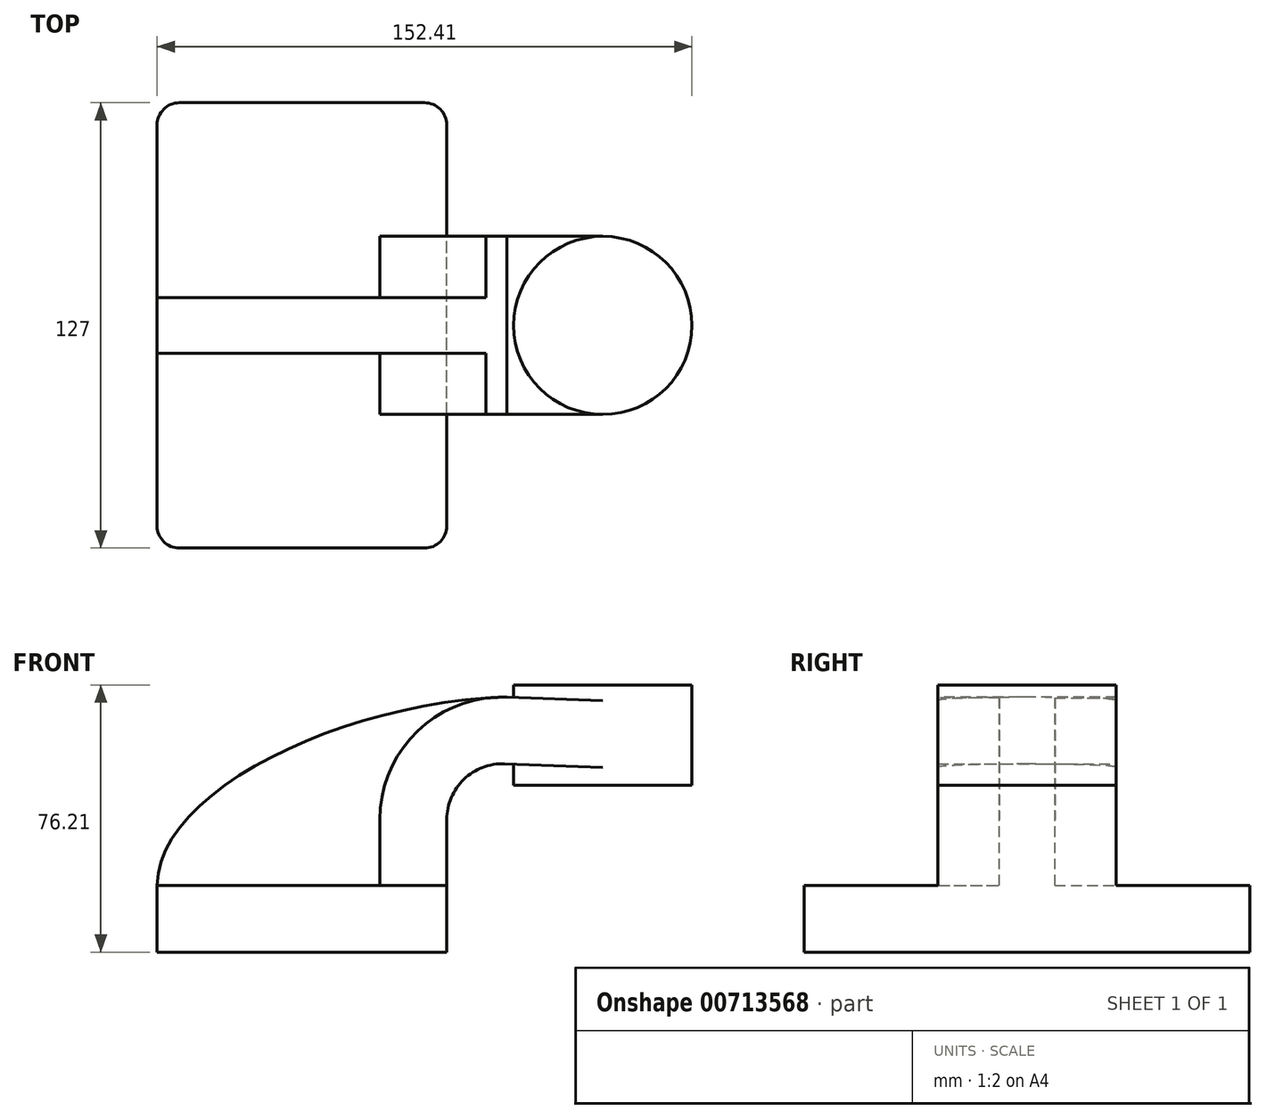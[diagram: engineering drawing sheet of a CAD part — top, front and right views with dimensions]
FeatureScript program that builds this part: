
annotation { "Feature Type Name" : "Feature", "Feature Type Description" : "" }
export const myFeature = defineFeature(function(context is Context, id is Id, definition is map)
    precondition{}
    {
        {
            var Q0;
            Q0=qCreatedBy(makeId("Front.planeOp"),FACE);
            var sketch = newSketch(context, id + "F0", { "sketchPlane" : qUnion([Q0])});
            skLineSegment(sketch, "E0.bottom", {"start": v(-41.28, -9.53) * mm, "end": v(41.28, -9.53) * mm});
            skLineSegment(sketch, "E0.top", {"start": v(-41.28, 9.53) * mm, "end": v(41.28, 9.53) * mm});
            skLineSegment(sketch, "E0.left", {"start": v(-41.28, -9.53) * mm, "end": v(-41.28, 9.53) * mm});
            skLineSegment(sketch, "E0.right", {"start": v(41.28, -9.53) * mm, "end": v(41.28, 9.53) * mm});
            skPoint(sketch, "E0.middle", {"position": v(0, 0) * mm});
            skLineSegment(sketch, "E1.bottom", {"start": v(60.33, 38.1) * mm, "end": v(111.13, 38.1) * mm});
            skLineSegment(sketch, "E1.top", {"start": v(60.32, 66.68) * mm, "end": v(111.12, 66.68) * mm});
            skLineSegment(sketch, "E1.left", {"start": v(60.33, 38.1) * mm, "end": v(60.32, 66.68) * mm});
            skLineSegment(sketch, "E1.right", {"start": v(111.13, 38.1) * mm, "end": v(111.12, 66.68) * mm});
            skPoint(sketch, "E1.middle", {"position": v(85.72, 52.39) * mm});
            skPoint(sketch, "E2.endSnap0", {"position": v(85.73, 38.1) * mm});
            skLineSegment(sketch, "E3", {"start": v(41.28, 9.53) * mm, "end": v(41.28, 22.09) * mm});
            skLineSegment(sketch, "E4", {"start": v(41.28, 22.09) * mm, "end": v(41.28, 28.31) * mm});
            skArc(sketch, "E5", {"start": v(41.28, 28.31) * mm, "mid": v(46.13, 39.74) * mm, "end": v(57.72, 44.18) * mm});
            skLineSegment(sketch, "E6", {"start": v(57.72, 44.18) * mm, "end": v(85.72, 43.17) * mm});
            skLineSegment(sketch, "E7.0", {"start": v(58.4, 63.21) * mm, "end": v(85.72, 62.23) * mm});
            skArc(sketch, "E7.1", {"start": v(22.23, 28.31) * mm, "mid": v(32.9, 53.45) * mm, "end": v(58.4, 63.21) * mm});
            skLineSegment(sketch, "E7.2", {"start": v(22.23, 22.09) * mm, "end": v(22.23, 28.31) * mm});
            skLineSegment(sketch, "E7.3", {"start": v(22.23, 9.53) * mm, "end": v(22.23, 22.09) * mm});
            skLineSegment(sketch, "E8", {"start": v(85.72, 38.1) * mm, "end": v(85.72, 66.68) * mm});
            skFitSpline(sketch, "E9", {"points": [v(-41.28, 9.53) * mm, v(58.4, 63.21) * mm], "startDerivative": vector(0.4, 81.2) * mm, "endDerivative": vector(139.39, 4.03) * mm});
            skSolve(sketch);
        }
        {
            var Q0;
            Q0=makeQuery(id+"F0.imprint","IMPRINT",FACE,{"disambiguationData":[TD([[makeQuery(id+"F0.imprint","IMPRINT",EDGE,{"derivedFrom":sQuery(id+"F0.wireOp",EDGE,"E0.bottom")}),1.0]])]});
            extrude(context, id + "F1", {"entities" : qUnion([Q0]), "endBound" : BoundingType.SYMMETRIC, "depth" : 127 * mm, "offsetDistance" : 25.4 * mm});
        }
        {
            var Q0;
            {var subQ12=sQuery(id+"F0.wireOp",EDGE,"E3");Q0=makeQuery(id+"F0.imprint","IMPRINT",FACE,{"disambiguationData":[TD([[makeQuery(id+"F0.imprint","IMPRINT",EDGE,{"derivedFrom":subQ12}),1.0]])]});}
            var Q1;
            {var subQ0=sQuery(id+"F0.wireOp",EDGE,"E6");var subQ1=sQuery(id+"F0.wireOp",EDGE,"E1.left");var subQ2=makeQuery(id+"F0.imprint","INTERSECT",VERTEX,{"derivedFrom":[subQ1,subQ0]});Q1=makeQuery(id+"F0.imprint","IMPRINT",FACE,{"disambiguationData":[TD([[makeQuery(id+"F0.imprint","IMPRINT",EDGE,{"disambiguationData":[TD([[subQ2,-1.0]])],"derivedFrom":subQ1}),-1.0]])]});}
            extrude(context, id + "F2", {"entities" : qUnion([Q0, Q1]), "operationType" : NewBodyOperationType.ADD, "endBound" : BoundingType.SYMMETRIC, "depth" : 50.8 * mm, "offsetDistance" : 25.4 * mm});
        }
        {
            var Q0;
            {var subQ4=sQuery(id+"F0.wireOp",EDGE,"E7.2");Q0=makeQuery(id+"F0.imprint","IMPRINT",FACE,{"disambiguationData":[TD([[makeQuery(id+"F0.imprint","IMPRINT",EDGE,{"derivedFrom":subQ4}),1.0]])]});}
            extrude(context, id + "F3", {"entities" : qUnion([Q0]), "operationType" : NewBodyOperationType.ADD, "endBound" : BoundingType.SYMMETRIC, "depth" : 15.88 * mm, "offsetDistance" : 25.4 * mm});
        }
        {
            var Q0;
            {var subQ4=sQuery(id+"F0.wireOp",EDGE,"E1.right");Q0=makeQuery(id+"F0.imprint","IMPRINT",FACE,{"disambiguationData":[TD([[makeQuery(id+"F0.imprint","IMPRINT",EDGE,{"derivedFrom":subQ4}),1.0]])]});}
            var Q1;
            Q1=sQuery(id+"F0.wireOp",EDGE,"E8");
            revolve(context, id + "F4", {"operationType" : NewBodyOperationType.ADD, "surfaceOperationType" : NewSurfaceOperationType.NEW, "entities" : qUnion([Q0]), "axis" : qUnion([Q1]), "revolveType" : RevolveType.FULL});
        }
        {
            var Q0;
            Q0=makeQuery(id+"F1.opExtrude","CAP_EDGE",EDGE,{"disambiguationData":[OSD([sQuery(id+"F0.wireOp",EDGE,"E0.right")])],"isStart":false});
            var Q1;
            Q1=makeQuery(id+"F1.opExtrude","CAP_EDGE",EDGE,{"disambiguationData":[OSD([sQuery(id+"F0.wireOp",EDGE,"E0.left")])],"isStart":false});
            var Q2;
            Q2=makeQuery(id+"F1.opExtrude","CAP_EDGE",EDGE,{"disambiguationData":[OSD([sQuery(id+"F0.wireOp",EDGE,"E0.left")])],"isStart":true});
            var Q3;
            Q3=makeQuery(id+"F1.opExtrude","CAP_EDGE",EDGE,{"disambiguationData":[OSD([sQuery(id+"F0.wireOp",EDGE,"E0.right")])],"isStart":true});
            fillet(context, id + "F5", {"entities" : qUnion([Q0, Q1, Q2, Q3]), "radius" : 6.35 * mm, "tangentPropagation" : true, "allowEdgeOverflow" : false});
        }
    });
